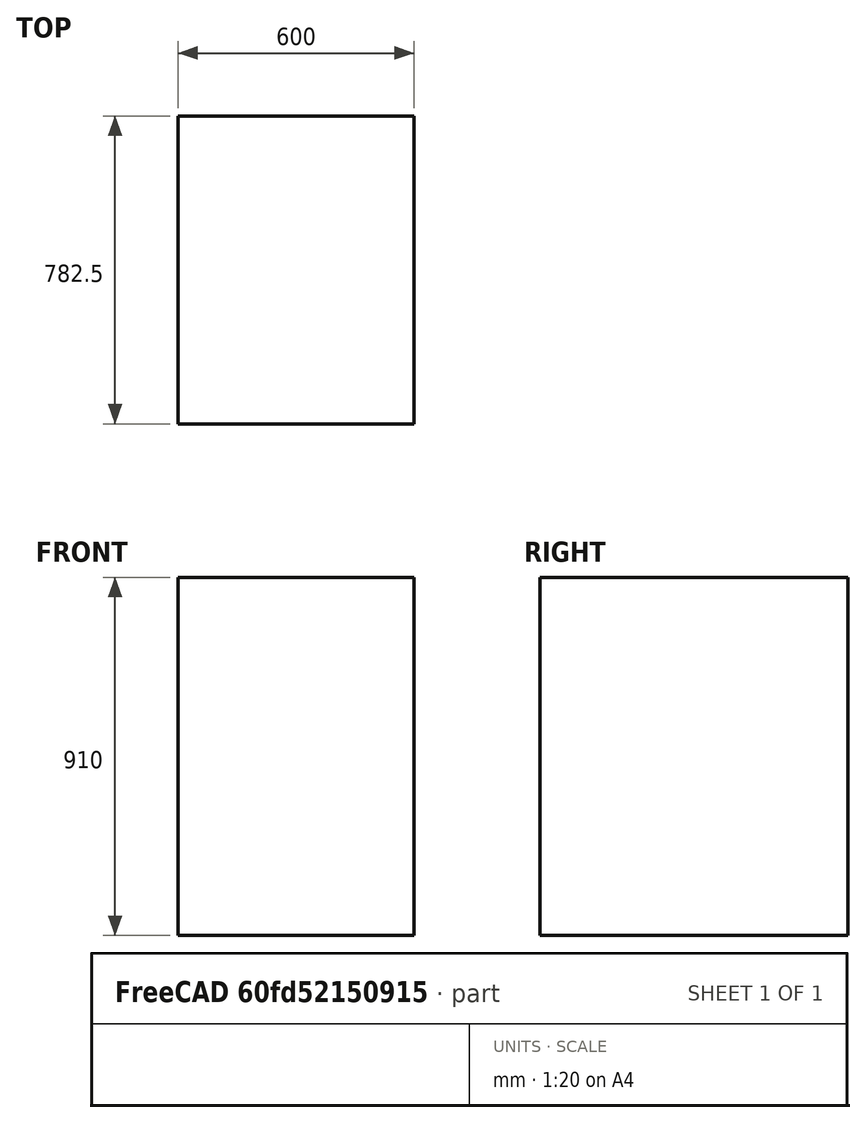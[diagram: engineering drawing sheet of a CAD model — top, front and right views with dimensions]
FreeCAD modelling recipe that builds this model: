
FCSTD DOCUMENT  (FreeCAD 0.19R24291 (Git))
Label: leftBuiltIn3-OneQuarter-tall
License: All rights reserved
LicenseURL: http://en.wikipedia.org/wiki/All_rights_reserved
objects: Sketcher::SketchObject×1, PartDesign::Pad×1, PartDesign::Body×1
note: 4 computed .brp shape members not serialized (recipe doc carries the construction recipe); baked Part::Feature solids carry a one-line shape summary decoded from their .brp

FEATURE [Sketcher::SketchObject] Sketch
  FullyConstrained = false
  MapMode = 5
  Placement = pos=(0,0,0) rot=(0.57735,0.57735,0.57735;2.0944rad)
  Support = -> [YZ_Plane]
  expr: Constraints[29] = 8 * 12 * 25.4
  expr: Constraints[8] = 3130 / 4
  sketch-geometry (12):
    g0: LineSegment StartX=-782.5 StartY=910 StartZ=0 EndX=0 EndY=910 EndZ=0
    g1: LineSegment StartX=0 StartY=910 StartZ=0 EndX=0 EndY=0 EndZ=0
    g2: LineSegment StartX=0 StartY=0 StartZ=0 EndX=-782.5 EndY=0 EndZ=0
    g3: LineSegment StartX=-782.5 StartY=0 StartZ=0 EndX=-782.5 EndY=910 EndZ=0
    g4: LineSegment StartX=-3667.4 StartY=1853.05 StartZ=0 EndX=-537.403 EndY=1853.05 EndZ=0
    g5: LineSegment StartX=-537.403 StartY=1853.05 StartZ=0 EndX=-537.403 EndY=1128.05 EndZ=0
    g6: LineSegment StartX=-537.403 StartY=1128.05 StartZ=0 EndX=-3667.4 EndY=1128.05 EndZ=0
    g7: LineSegment StartX=-3667.4 StartY=1128.05 StartZ=0 EndX=-3667.4 EndY=1853.05 EndZ=0
    g8: LineSegment StartX=-3581.05 StartY=2612.82 StartZ=0 EndX=-1142.65 EndY=2612.82 EndZ=0
    g9: LineSegment StartX=-1142.65 StartY=2612.82 StartZ=0 EndX=-1142.65 EndY=2361.64 EndZ=0
    g10: LineSegment StartX=-1142.65 StartY=2361.64 StartZ=0 EndX=-3581.05 EndY=2361.64 EndZ=0
    g11: LineSegment StartX=-3581.05 StartY=2361.64 StartZ=0 EndX=-3581.05 EndY=2612.82 EndZ=0
  constraints (30):
    c: Coincident(g0,g1)
    c: Coincident(g1,g2)
    c: Coincident(g2,g3)
    c: Coincident(g3,g0)
    c: Horizontal(g0)
    c: Horizontal(g2)
    c: Vertical(g1)
    c: Vertical(g3)
    c: DistanceX(g2,g2) = 782.5
    c: DistanceY(g3,g3) = 910
    c: Coincident(g4,g5)
    c: Coincident(g5,g6)
    c: Coincident(g6,g7)
    c: Coincident(g7,g4)
    c: Horizontal(g4)
    c: Horizontal(g6)
    c: Vertical(g5)
    c: Vertical(g7)
    c: DistanceY(g7,g7) = 725
    c: DistanceX(g6,g6) = 3130
    c: Coincident(g1,g-1)
    c: Coincident(g8,g9)
    c: Coincident(g9,g10)
    c: Coincident(g10,g11)
    c: Coincident(g11,g8)
    c: Horizontal(g8)
    c: Horizontal(g10)
    c: Vertical(g9)
    c: Vertical(g11)
    c: DistanceX(g10,g10) = 2438.4
FEATURE [PartDesign::Pad] Pad
  Direction = (1,1,1)
  Length = 600
  Length2 = 100
  Placement = pos=(0,0,0) rot=(0.57735,0.57735,0.57735;2.0944rad)
  Profile = -> Sketch
  Type = 0
FEATURE [PartDesign::Body] Body
  Group = -> [Sketch,Pad]
  Origin = -> Origin
  Tip = -> Pad
